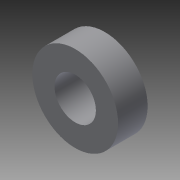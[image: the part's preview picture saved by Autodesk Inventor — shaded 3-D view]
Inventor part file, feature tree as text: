
AUTODESK INVENTOR PART (.ipt)
format: ipt  version: 2013 (Build 170138000, 138)  size: 77,824 bytes
history: native  units: in
note: dims shown in document units (in); Inventor stores cm internally (conversion verified against a paired STEP export)
features: extrude x1, sketch x1
ambient origin geometry x8: Origin, YZ Plane, XZ Plane, XY Plane, X Axis, Y Axis, Z Axis, Center Point
bodies: Solid1 (feature_tree)
feature tree (2):
  extrude  "Extrusion1"  Depth=0.9063in
  sketch  "Sketch1"  dims[d0=0.4375in d2=0.9063in d3=0.3125in d4=0.0in]
